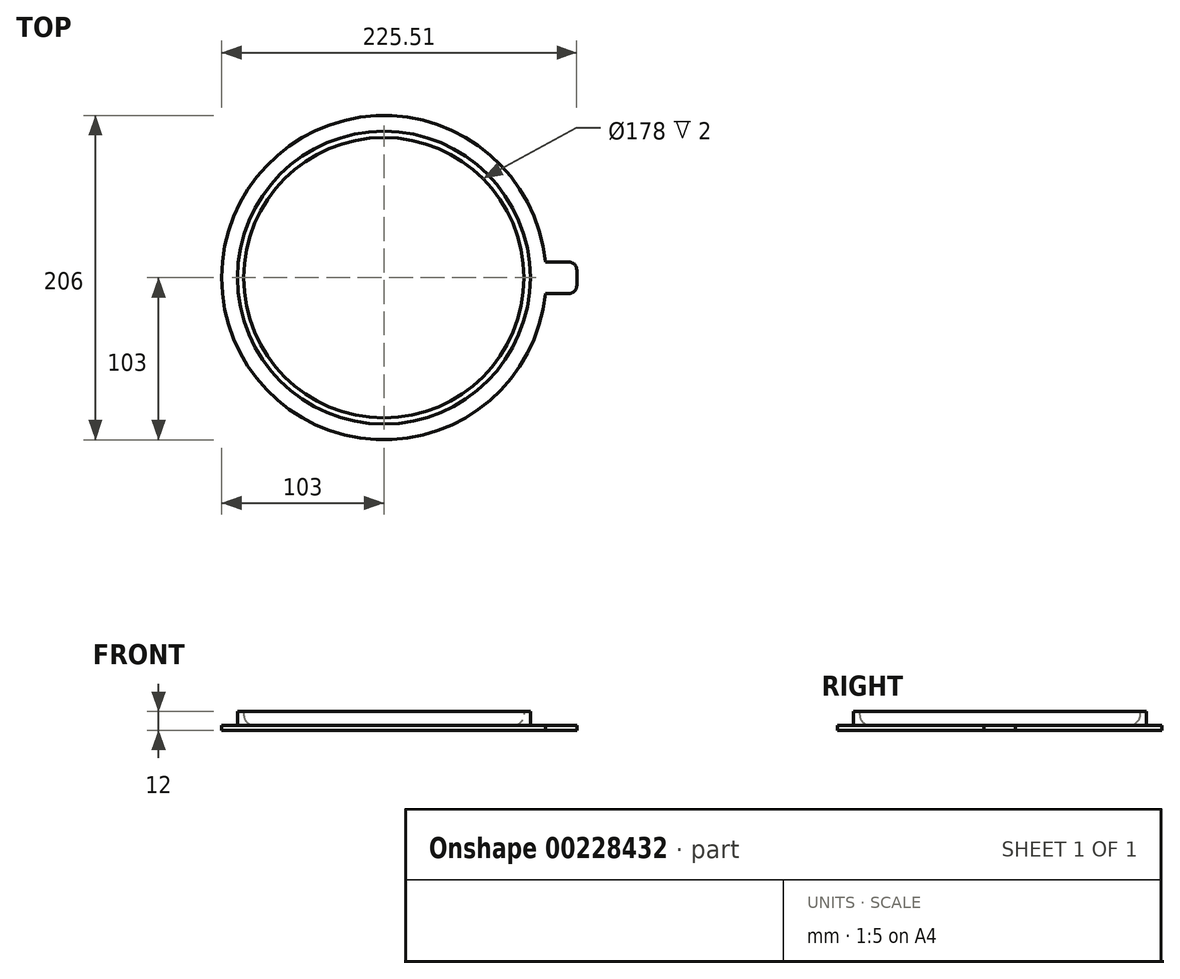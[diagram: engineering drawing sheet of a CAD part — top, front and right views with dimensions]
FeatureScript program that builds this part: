
annotation { "Feature Type Name" : "Feature", "Feature Type Description" : "" }
export const myFeature = defineFeature(function(context is Context, id is Id, definition is map)
    precondition{}
    {
        {
            var Q0;
            Q0=qCreatedBy(makeId("Top.planeOp"),FACE);
            var sketch = newSketch(context, id + "F0", { "sketchPlane" : qUnion([Q0])});
            skCircle(sketch, "E0", {"center": v(0, 0) * mm, "radius": 93 * mm});
            skCircle(sketch, "E1.0", {"center": v(0, 0) * mm, "radius": 89 * mm});
            skCircle(sketch, "E2.0", {"center": v(0, 0) * mm, "radius": 103 * mm});
            skLineSegment(sketch, "E3", {"start": v(0, 0) * mm, "end": v(152.77, 0) * mm, "construction": true});
            skLineSegment(sketch, "E4", {"start": v(102.51, 10) * mm, "end": v(117.51, 10) * mm});
            skLineSegment(sketch, "E5", {"start": v(122.51, 5) * mm, "end": v(122.51, 0) * mm});
            skLineSegment(sketch, "E6.MirrorCS", {"start": v(122.51, -5) * mm, "end": v(122.51, 0) * mm});
            skLineSegment(sketch, "E7.MirrorCS", {"start": v(102.51, -10) * mm, "end": v(117.51, -10) * mm});
            skPoint(sketch, "E8.visualSharp", {"position": v(122.51, 10) * mm});
            skArc(sketch, "E8.filletArc", {"start": v(122.51, 5) * mm, "mid": v(121.05, 8.54) * mm, "end": v(117.51, 10) * mm});
            skPoint(sketch, "E9.visualSharp", {"position": v(122.51, -10) * mm});
            skArc(sketch, "E9.filletArc", {"start": v(117.51, -10) * mm, "mid": v(121.05, -8.54) * mm, "end": v(122.51, -5) * mm});
            skSolve(sketch);
        }
        {
            var Q0;
            Q0=makeQuery(id+"F0.imprint","IMPRINT",FACE,{"disambiguationData":[TD([[makeQuery(id+"F0.imprint","IMPRINT",EDGE,{"derivedFrom":sQuery(id+"F0.wireOp",EDGE,"E0")}),-1.0]])]});
            var Q1;
            Q1=makeQuery(id+"F0.imprint","IMPRINT",FACE,{"disambiguationData":[TD([[makeQuery(id+"F0.imprint","IMPRINT",EDGE,{"derivedFrom":sQuery(id+"F0.wireOp",EDGE,"E0")}),1.0]])]});
            var Q2;
            Q2=makeQuery(id+"F0.imprint","IMPRINT",FACE,{"disambiguationData":[TD([[makeQuery(id+"F0.imprint","IMPRINT",EDGE,{"derivedFrom":sQuery(id+"F0.wireOp",EDGE,"E1.0")}),1.0]])]});
            var Q3;
            {var subQ0=sQuery(id+"F0.wireOp",EDGE,"E4");Q3=makeQuery(id+"F0.imprint","IMPRINT",FACE,{"disambiguationData":[TD([[makeQuery(id+"F0.imprint","IMPRINT",EDGE,{"derivedFrom":subQ0}),-1.0]])]});}
            extrude(context, id + "F1", {"entities" : qUnion([Q0, Q1, Q2, Q3]), "depth" : 3 * mm, "offsetDistance" : 25 * mm});
        }
        {
            var Q0;
            Q0=makeQuery(id+"F0.imprint","IMPRINT",FACE,{"disambiguationData":[TD([[makeQuery(id+"F0.imprint","IMPRINT",EDGE,{"derivedFrom":sQuery(id+"F0.wireOp",EDGE,"E0")}),1.0]])]});
            extrude(context, id + "F2", {"entities" : qUnion([Q0]), "operationType" : NewBodyOperationType.ADD, "depth" : 12 * mm, "offsetDistance" : 25 * mm});
        }
        {
            var Q0;
            Q0=makeQuery(id+"F2.boolean.opBoolean","INTERSECT",EDGE,{"derivedFrom":[makeQuery(id+"F1.opExtrude","CAP_FACE",FACE,{"disambiguationData":[OSD([sQuery(id+"F0.wireOp",EDGE,"E2.0")])],"isStart":false}),makeQuery(id+"F2.opExtrude","SWEPT_FACE",FACE,{"disambiguationData":[OSD([sQuery(id+"F0.wireOp",EDGE,"E1.0")])]})]});
            fillet(context, id + "F3", {"entities" : qUnion([Q0]), "radius" : 7 * mm, "tangentPropagation" : true, "allowEdgeOverflow" : false});
        }
    });
